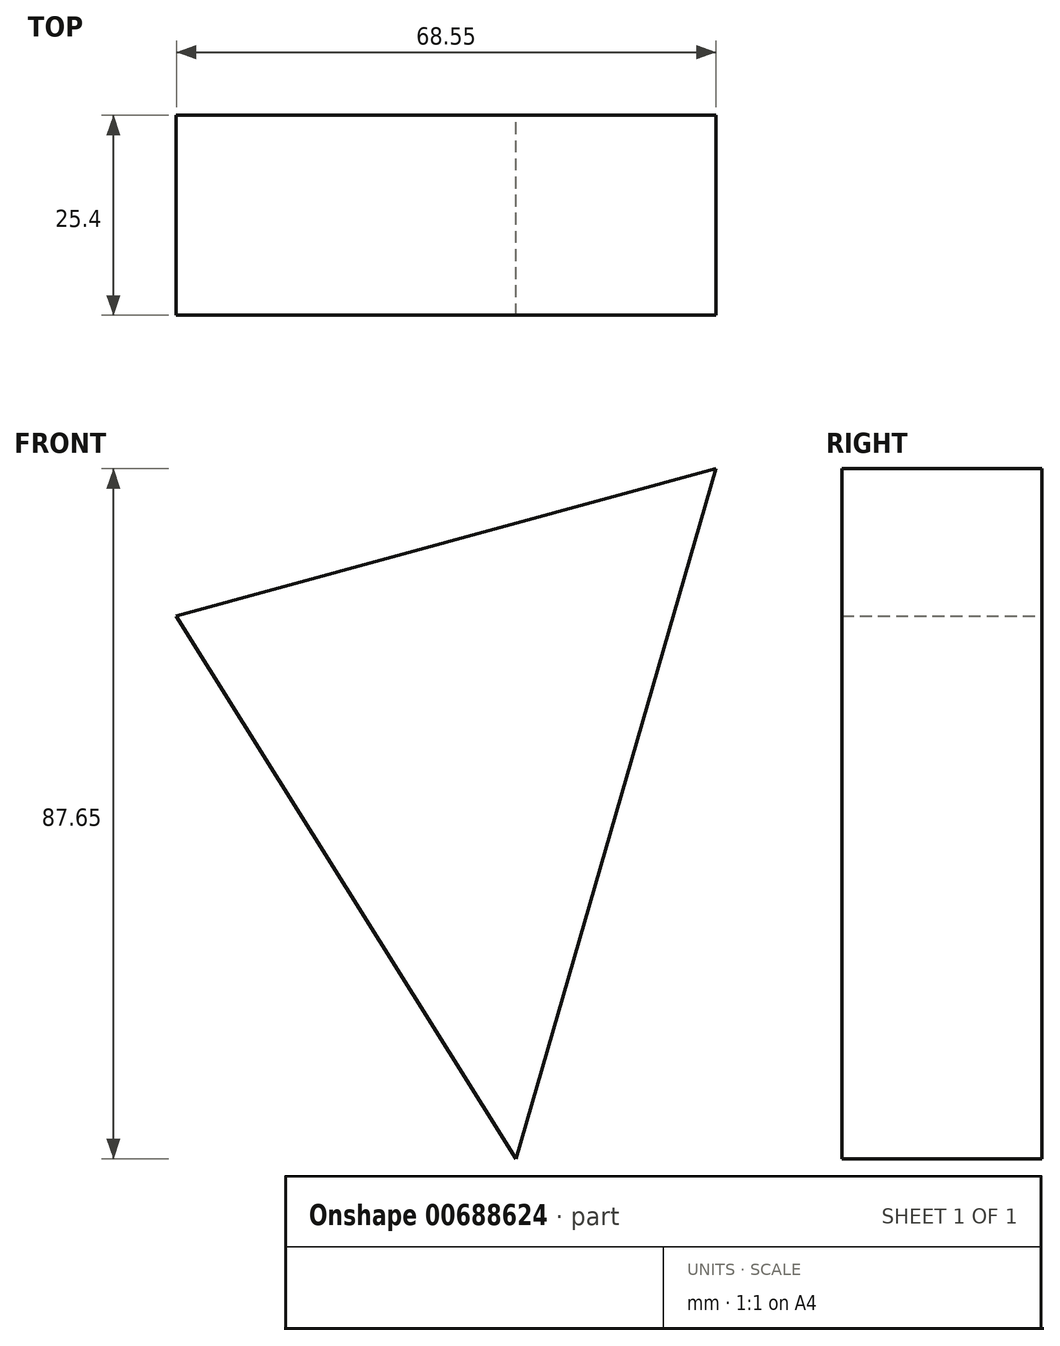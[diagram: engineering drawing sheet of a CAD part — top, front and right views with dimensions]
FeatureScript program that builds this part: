
annotation { "Feature Type Name" : "Feature", "Feature Type Description" : "" }
export const myFeature = defineFeature(function(context is Context, id is Id, definition is map)
    precondition{}
    {
        {
            var Q0;
            Q0=qCreatedBy(makeId("Front.planeOp"),FACE);
            var sketch = newSketch(context, id + "F0", { "sketchPlane" : qUnion([Q0])});
            skLineSegment(sketch, "E0", {"start": v(-35.23, 37.71) * mm, "end": v(7.92, -31.22) * mm});
            skLineSegment(sketch, "E1", {"start": v(7.92, -31.22) * mm, "end": v(33.32, 56.43) * mm});
            skLineSegment(sketch, "E2", {"start": v(33.32, 56.43) * mm, "end": v(-35.23, 37.71) * mm});
            skSolve(sketch);
        }
        {
            var Q0;
            Q0 = qSketchRegion(id + "F0", true);
            extrude(context, id + "F1", {"entities" : qUnion([Q0]), "depth" : 25.4 * mm, "offsetDistance" : 25.4 * mm});
        }
    });
